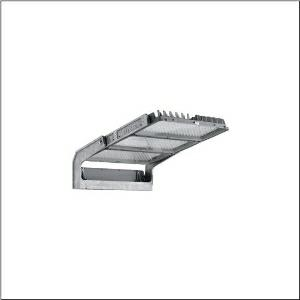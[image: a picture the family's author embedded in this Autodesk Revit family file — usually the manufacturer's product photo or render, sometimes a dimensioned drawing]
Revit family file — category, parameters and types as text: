
# Revit family: floodlight_fl_11_maxi_pro___rs07_5xa779229k01gb_e668
name_source: partatom
category: Lighting Fixtures
units: mm (PartAtom-declared; Revit-internal decimal feet)

## family parameters
Cut with Voids When Loaded = No
Host = Face
Light Source = No
Part Type = Normal
Room Calculation Point = No
Round Connector Dimension = Use Diameter
Shared = No

## types (1)
- --- (1 x LED, 164870 lm, 1315 W, 5700K)
    Apparent Load = 1315 VA
    CIE Flux Codes = 80 93 99 100 99
    Color Rendering = 70
    Color Temperature = 5700K
    Default Elevation = 1800 mm
    Description = Floodlight FL 11  maxi  pro floodlight; light control with lens of PMMA; cover panel of toughened safety glass, transparent; light distribution: RS07, rotationally symmetric direct distribution, LEDcolour temperature: 5700K, rated luminous flux: 164.870lm, colour rendering: CRI > 70, light colour: 757; luminous efficacy: 125lm/W; brightness control: DMX+RDM; with terminal, 5-pole, max. 2.5mm², mains connection: 220..240V/380..400V AC, 50/60Hz, surge voltage resistance: line to ground: 10kV, service life up to 100,000h L90. Typical operating time: 1000h per year, ECG replaceable separately, LED unit replaceable without ESD environment, dustproof LED module, dimming range 10..100%; 1315W floodlight with 3x LED unit of diecast aluminium, coated grey; length: 1.003mm / width: 651mm / height: 338mm; mounting bracket, of diecast aluminium, uncoated, natural, protection rating (complete): IP66; insulation class (complete): insulation class I (protective earthing); certification: CE, ENEC, VDE; ball protection: ball impact resistant, only for outdoor installations in the designated locations, permissible operating ambient temperature: -45..+55°C, permissible storage temperature: -40..+85°Cpackaging unit: 1 piece

Light Distribution: RS07
    Height = 320 mm
    Lamp = 1 x LED
    Lamp Light Flux = 164870 lm
    Lamp Power = 1315 W
    Lamp count = 1
    Length = 1002 mm
    Luminous efficacy = 125 lm/W
    Manufacturer = Siteco
    ModVariant = No
    Model = 5XA779229K01GB
    Mounting Place = Ceiling
    Mounting Type = Surface mounted
    Number of Poles = 1
    OnlyDefault = Yes
    Power Factor = 1
    Product Name = Floodlight FL 11 maxi pro | RS07
    Product group = floodlight | ceiling mounted
    ProductGroupID = 301
    Protection Class = Protection class I
    Protection Degree = IP 66
    RLX_Detail_Level = 1
    RLX_Emergency_Light_Flux = 0 lm
    RLX_Emergency_Type = 0
    RLX_Emergency_Type_DB = No
    RlxData = <blob elided: 40333 chars, md5=48aa4f8a>
    Socket = socket
    Standby Power = 0 W
    System Light Flux = 164870 lm
    System Power = 1315 W
    Type Comments = factory setting: luminous flux: 100 % | dim-lin: 255 | 895 mA
    Type Image = l_1356210.jpg
    URL = http://relux.com
    VarID = @adj_013881
    Voltage = 0 V
    Weight = 0.00 kg
    Width = 655 mm

## geometry (parser evidence)
native form markers: Blend x4, Sweep x11
no freeform markers — native parametric forms only
